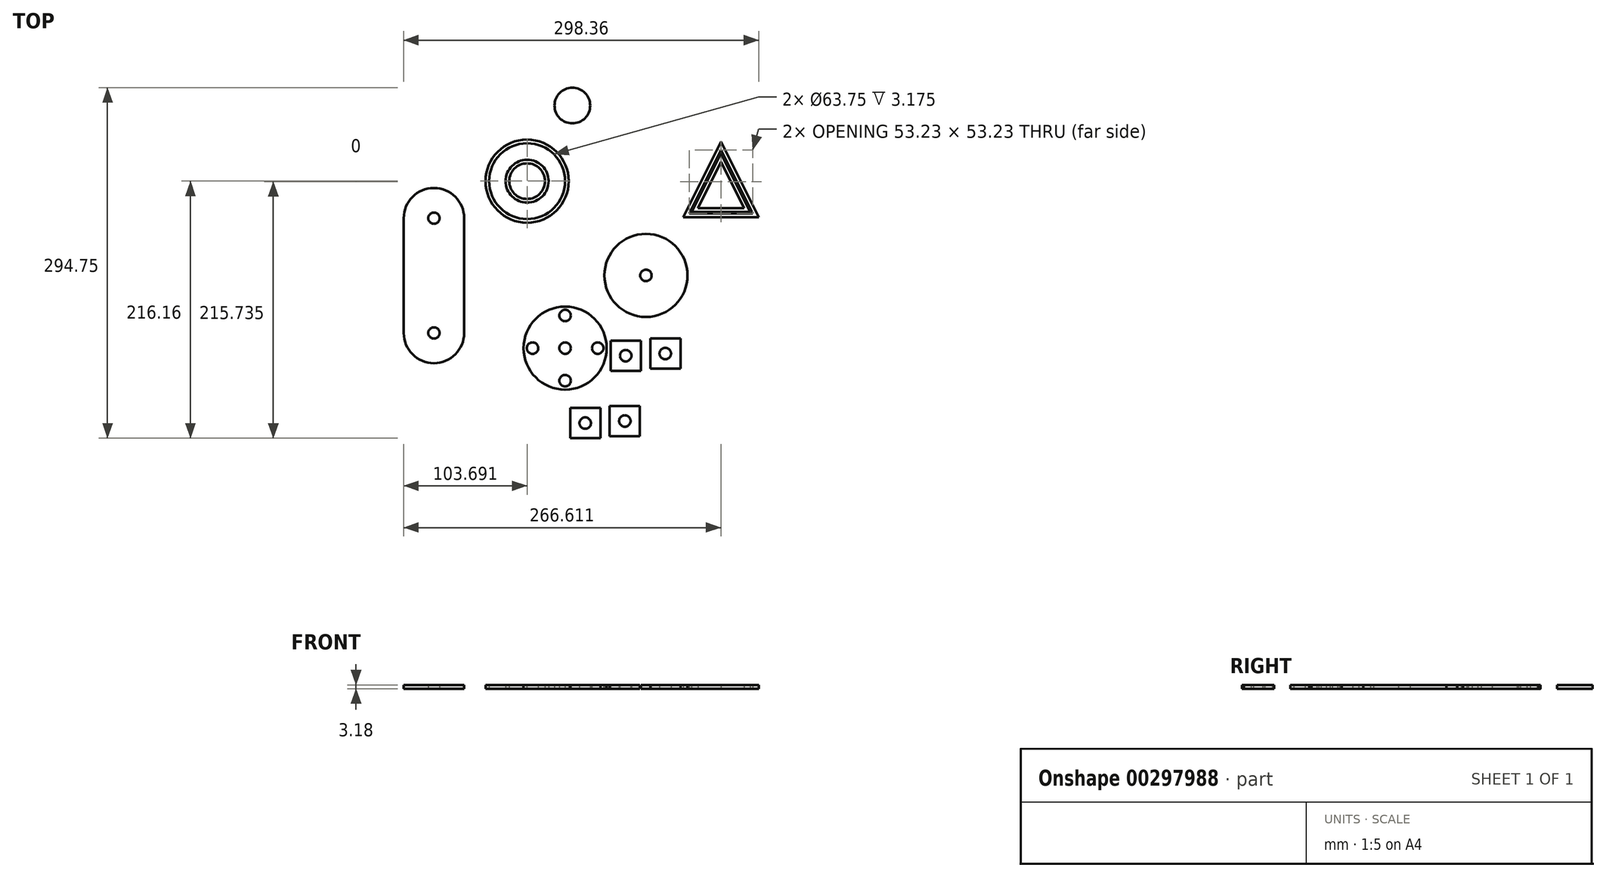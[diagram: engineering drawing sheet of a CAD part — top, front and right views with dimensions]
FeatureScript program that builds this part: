
annotation { "Feature Type Name" : "Feature", "Feature Type Description" : "" }
export const myFeature = defineFeature(function(context is Context, id is Id, definition is map)
    precondition{}
    {
        {
            var Q0;
            Q0=qCreatedBy(makeId("Top.planeOp"),FACE);
            var sketch = newSketch(context, id + "F0", { "sketchPlane" : qUnion([Q0])});
            skLineSegment(sketch, "E0", {"start": v(57.75, 2.39) * mm, "end": v(121.25, 2.39) * mm});
            skLineSegment(sketch, "E1", {"start": v(57.75, 2.39) * mm, "end": v(89.5, 65.89) * mm});
            skPoint(sketch, "E1.endSnap0", {"position": v(89.5, 2.39) * mm});
            skLineSegment(sketch, "E2", {"start": v(89.5, 65.89) * mm, "end": v(121.25, 2.39) * mm});
            skLineSegment(sketch, "E3", {"start": v(116.11, 5.56) * mm, "end": v(89.5, 58.79) * mm});
            skLineSegment(sketch, "E4", {"start": v(62.89, 5.56) * mm, "end": v(116.11, 5.56) * mm});
            skLineSegment(sketch, "E5", {"start": v(89.5, 58.79) * mm, "end": v(62.89, 5.56) * mm});
            skLineSegment(sketch, "E6", {"start": v(64.94, 6.83) * mm, "end": v(114.06, 6.83) * mm});
            skLineSegment(sketch, "E7", {"start": v(64.94, 6.83) * mm, "end": v(89.5, 55.95) * mm});
            skLineSegment(sketch, "E8", {"start": v(89.5, 55.95) * mm, "end": v(114.06, 6.83) * mm});
            skLineSegment(sketch, "E9", {"start": v(70.08, 10) * mm, "end": v(89.5, 48.85) * mm});
            skLineSegment(sketch, "E10", {"start": v(89.5, 48.85) * mm, "end": v(108.92, 10) * mm});
            skLineSegment(sketch, "E11", {"start": v(108.92, 10) * mm, "end": v(70.08, 10) * mm});
            skPoint(sketch, "E12.start.orphan", {"position": v(76.2, 32.18) * mm});
            skPoint(sketch, "E13.end.orphan", {"position": v(89.5, 5.56) * mm});
            skPoint(sketch, "E14.end.orphan", {"position": v(80.88, 6.83) * mm});
            skPoint(sketch, "E15.end.orphan", {"position": v(94.24, 10) * mm});
            skCircle(sketch, "E16", {"center": v(-73.42, 32.6) * mm, "radius": 34.95 * mm});
            skCircle(sketch, "E17", {"center": v(-73.42, 32.6) * mm, "radius": 31.88 * mm});
            skLineSegment(sketch, "E18", {"start": v(89.5, 48.85) * mm, "end": v(89.5, 10) * mm});
            skCircle(sketch, "E19", {"center": v(-73.42, 32.6) * mm, "radius": 18.03 * mm});
            skCircle(sketch, "E20", {"center": v(-73.42, 32.6) * mm, "radius": 14.99 * mm});
            skLineSegment(sketch, "E21", {"start": v(89.5, 2.39) * mm, "end": v(89.5, 5.56) * mm});
            skLineSegment(sketch, "E22", {"start": v(89.5, 6.83) * mm, "end": v(89.5, 48.85) * mm});
            skCircle(sketch, "E23", {"center": v(-35.38, 96.2) * mm, "radius": 14.99 * mm});
            skSolve(sketch);
        }
        {
            var Q0;
            Q0=qCreatedBy(makeId("Top.planeOp"),FACE);
            var sketch = newSketch(context, id + "F1", { "sketchPlane" : qUnion([Q0])});
            skCircle(sketch, "E24", {"center": v(-41.46, -107.8) * mm, "radius": 34.93 * mm});
            skCircle(sketch, "E25", {"center": v(-41.46, -107.8) * mm, "radius": 4.83 * mm});
            skPoint(sketch, "E26.orphan", {"position": v(-46.28, -107.8) * mm});
            skPoint(sketch, "E27.orphan", {"position": v(-36.63, -107.8) * mm});
            skPoint(sketch, "E28.orphan", {"position": v(-41.46, -112.63) * mm});
            skPoint(sketch, "E29.orphan", {"position": v(-41.46, -102.98) * mm});
            skPoint(sketch, "E30", {"position": v(-41.46, -135.2) * mm});
            skPoint(sketch, "E31", {"position": v(-14.06, -107.8) * mm});
            skPoint(sketch, "E32", {"position": v(-41.46, -80.4) * mm});
            skPoint(sketch, "E33", {"position": v(-68.86, -107.8) * mm});
            skPoint(sketch, "E34.trimOffspring.end.orphan", {"position": v(-76.38, -107.8) * mm});
            skPoint(sketch, "E35.end.orphan", {"position": v(-41.46, -72.88) * mm});
            skPoint(sketch, "E36.end.orphan", {"position": v(-6.53, -107.8) * mm});
            skPoint(sketch, "E37.trimOffspring.end.orphan", {"position": v(-41.46, -142.73) * mm});
            skCircle(sketch, "E38", {"center": v(-41.46, -135.2) * mm, "radius": 4.83 * mm});
            skCircle(sketch, "E39", {"center": v(-14.06, -107.8) * mm, "radius": 4.83 * mm});
            skCircle(sketch, "E40", {"center": v(-41.46, -80.4) * mm, "radius": 4.83 * mm});
            skCircle(sketch, "E41", {"center": v(-68.86, -107.8) * mm, "radius": 4.83 * mm});
            skLineSegment(sketch, "E42", {"start": v(-41.46, -112.63) * mm, "end": v(-41.46, -102.98) * mm});
            skSolve(sketch);
        }
        {
            var Q0;
            Q0=makeQuery(id+"F1.imprint","IMPRINT",FACE,{"disambiguationData":[TD([[makeQuery(id+"F1.imprint","IMPRINT",EDGE,{"derivedFrom":sQuery(id+"F1.wireOp",EDGE,"E24")}),1.0]])]});
            extrude(context, id + "F2", {"entities" : qUnion([Q0]), "depth" : 3.17 * mm});
        }
        {
            var Q0;
            Q0=qCreatedBy(makeId("Top.planeOp"),FACE);
            var sketch = newSketch(context, id + "F3", { "sketchPlane" : qUnion([Q0])});
            skCircle(sketch, "E43", {"center": v(26.47, -46.67) * mm, "radius": 34.93 * mm});
            skSolve(sketch);
        }
        {
            var Q0;
            Q0=makeQuery(id+"F3.imprint","IMPRINT",FACE,{"disambiguationData":[TD([[makeQuery(id+"F3.imprint","IMPRINT",EDGE,{"derivedFrom":sQuery(id+"F3.wireOp",EDGE,"E43")}),1.0]])]});
            extrude(context, id + "F4", {"entities" : qUnion([Q0]), "depth" : 3.17 * mm});
        }
        {
            var Q0;
            Q0=makeQuery(id+"F4.opExtrude","CAP_FACE",FACE,{"disambiguationData":[OSD([sQuery(id+"F3.wireOp",EDGE,"E43")])],"isStart":false});
            var sketch = newSketch(context, id + "F5", { "sketchPlane" : qUnion([Q0])});
            skPoint(sketch, "E44", {"position": v(26.47, -46.67) * mm});
            skCircle(sketch, "E45", {"center": v(26.47, -46.67) * mm, "radius": 4.83 * mm});
            skSolve(sketch);
        }
        {
            var Q0;
            Q0=makeQuery(id+"F5.imprint","IMPRINT",FACE,{"disambiguationData":[TD([[makeQuery(id+"F5.imprint","IMPRINT",EDGE,{"derivedFrom":sQuery(id+"F5.wireOp",EDGE,"E45")}),1.0]])]});
            extrude(context, id + "F6", {"entities" : qUnion([Q0]), "operationType" : NewBodyOperationType.REMOVE, "oppositeDirection" : true, "depth" : 25.4 * mm});
        }
        {
            var Q0;
            Q0=qCreatedBy(makeId("Top.planeOp"),FACE);
            var sketch = newSketch(context, id + "F7", { "sketchPlane" : qUnion([Q0])});
            skLineSegment(sketch, "E46.bottom", {"start": v(-3.27, -101.45) * mm, "end": v(22.13, -101.45) * mm});
            skLineSegment(sketch, "E46.top", {"start": v(-3.27, -126.85) * mm, "end": v(22.13, -126.85) * mm});
            skLineSegment(sketch, "E46.left", {"start": v(-3.27, -101.45) * mm, "end": v(-3.27, -126.85) * mm});
            skLineSegment(sketch, "E46.right", {"start": v(22.13, -101.45) * mm, "end": v(22.13, -126.85) * mm});
            skPoint(sketch, "E47", {"position": v(9.43, -114.15) * mm});
            skCircle(sketch, "E48", {"center": v(9.43, -114.15) * mm, "radius": 4.83 * mm});
            skLineSegment(sketch, "E49.MirrorCS", {"start": v(30.02, -99.66) * mm, "end": v(30.02, -125.06) * mm});
            skLineSegment(sketch, "E50.MirrorCS", {"start": v(55.42, -99.66) * mm, "end": v(30.02, -99.66) * mm});
            skLineSegment(sketch, "E51.MirrorCS", {"start": v(55.42, -125.06) * mm, "end": v(30.02, -125.06) * mm});
            skLineSegment(sketch, "E52.MirrorCS", {"start": v(55.42, -99.66) * mm, "end": v(55.42, -125.06) * mm});
            skPoint(sketch, "E53", {"position": v(42.72, -112.36) * mm});
            skCircle(sketch, "E54", {"center": v(42.72, -112.36) * mm, "radius": 4.83 * mm});
            skLineSegment(sketch, "E55.bottom", {"start": v(-37.27, -158.16) * mm, "end": v(-11.87, -158.16) * mm});
            skLineSegment(sketch, "E55.top", {"start": v(-37.27, -183.56) * mm, "end": v(-11.87, -183.56) * mm});
            skLineSegment(sketch, "E55.left", {"start": v(-37.27, -158.16) * mm, "end": v(-37.27, -183.56) * mm});
            skLineSegment(sketch, "E55.right", {"start": v(-11.87, -158.16) * mm, "end": v(-11.87, -183.56) * mm});
            skPoint(sketch, "E56", {"position": v(-24.57, -170.86) * mm});
            skCircle(sketch, "E57", {"center": v(-24.57, -170.86) * mm, "radius": 4.83 * mm});
            skLineSegment(sketch, "E58.MirrorCS", {"start": v(-3.97, -156.37) * mm, "end": v(-3.97, -181.77) * mm});
            skLineSegment(sketch, "E59.MirrorCS", {"start": v(21.43, -156.37) * mm, "end": v(-3.97, -156.37) * mm});
            skLineSegment(sketch, "E60.MirrorCS", {"start": v(21.43, -181.77) * mm, "end": v(-3.97, -181.77) * mm});
            skLineSegment(sketch, "E61.MirrorCS", {"start": v(21.43, -156.37) * mm, "end": v(21.43, -181.77) * mm});
            skPoint(sketch, "E62", {"position": v(8.73, -169.07) * mm});
            skCircle(sketch, "E63", {"center": v(8.73, -169.07) * mm, "radius": 4.83 * mm});
            skSolve(sketch);
        }
        {
            var Q0;
            Q0=makeQuery(id+"F7.imprint","IMPRINT",FACE,{"disambiguationData":[TD([[makeQuery(id+"F7.imprint","IMPRINT",EDGE,{"derivedFrom":sQuery(id+"F7.wireOp",EDGE,"E46.bottom")}),-1.0]])]});
            var Q1;
            Q1=makeQuery(id+"F7.imprint","IMPRINT",FACE,{"disambiguationData":[TD([[makeQuery(id+"F7.imprint","IMPRINT",EDGE,{"derivedFrom":sQuery(id+"F7.wireOp",EDGE,"xvH5cVz1-pj4Y-tES7-m2WN-IS9xY6hBvVlf.bottom")}),-1.0]])]});
            var Q2;
            Q2=makeQuery(id+"F7.imprint","IMPRINT",FACE,{"disambiguationData":[TD([[makeQuery(id+"F7.imprint","IMPRINT",EDGE,{"derivedFrom":sQuery(id+"F7.wireOp",EDGE,"6ae7865e-581d-49da-b914-e63cb27099890.MirrorC")}),1.0]])]});
            extrude(context, id + "F8", {"entities" : qUnion([Q0, Q1, Q2]), "depth" : 3.17 * mm});
        }
        {
            var Q0;
            Q0=makeQuery(id+"F0.imprint","IMPRINT",FACE,{"disambiguationData":[TD([[makeQuery(id+"F0.imprint","IMPRINT",EDGE,{"derivedFrom":sQuery(id+"F0.wireOp",EDGE,"E19")}),1.0]])]});
            var Q1;
            Q1=makeQuery(id+"F0.imprint","IMPRINT",FACE,{"disambiguationData":[TD([[makeQuery(id+"F0.imprint","IMPRINT",EDGE,{"derivedFrom":sQuery(id+"F0.wireOp",EDGE,"E16")}),1.0]])]});
            var Q2;
            Q2=makeQuery(id+"F0.imprint","IMPRINT",FACE,{"disambiguationData":[TD([[makeQuery(id+"F0.imprint","IMPRINT",EDGE,{"derivedFrom":sQuery(id+"F0.wireOp",EDGE,"E0")}),1.0]])]});
            var Q3;
            Q3=makeQuery(id+"F0.imprint","IMPRINT",FACE,{"disambiguationData":[TD([[makeQuery(id+"F0.imprint","IMPRINT",EDGE,{"derivedFrom":sQuery(id+"F0.wireOp",EDGE,"E6")}),1.0]])]});
            extrude(context, id + "F9", {"entities" : qUnion([Q0, Q1, Q2, Q3]), "depth" : 3.17 * mm});
        }
        {
            var Q0;
            Q0=qCreatedBy(makeId("Top.planeOp"),FACE);
            var sketch = newSketch(context, id + "F10", { "sketchPlane" : qUnion([Q0])});
            skArc(sketch, "E64", {"start": v(-126.31, 1.47) * mm, "mid": v(-151.71, 26.87) * mm, "end": v(-177.11, 1.47) * mm});
            skLineSegment(sketch, "E65", {"start": v(-177.11, 1.47) * mm, "end": v(-177.11, -95.05) * mm});
            skArc(sketch, "E66", {"start": v(-177.11, -95.05) * mm, "mid": v(-151.71, -120.45) * mm, "end": v(-126.31, -95.05) * mm});
            skLineSegment(sketch, "E67", {"start": v(-126.31, 1.47) * mm, "end": v(-126.31, -95.05) * mm});
            skCircle(sketch, "E68", {"center": v(-151.71, 1.47) * mm, "radius": 4.76 * mm});
            skCircle(sketch, "E69", {"center": v(-151.71, -95.05) * mm, "radius": 4.76 * mm});
            skSolve(sketch);
        }
        {
            var Q0;
            Q0=makeQuery(id+"F10.imprint","IMPRINT",FACE,{"disambiguationData":[TD([[makeQuery(id+"F10.imprint","IMPRINT",EDGE,{"derivedFrom":sQuery(id+"F10.wireOp",EDGE,"E64")}),1.0]])]});
            extrude(context, id + "F11", {"entities" : qUnion([Q0]), "depth" : 3.17 * mm});
        }
        {
            var Q0;
            Q0=qSketchRegion(id+"F7",true);
            extrude(context, id + "F12", {"entities" : qUnion([Q0]), "operationType" : NewBodyOperationType.ADD, "depth" : 3.17 * mm});
        }
        {
            var Q0;
            Q0=qSketchRegion(id+"F0",true);
            extrude(context, id + "F13", {"entities" : qUnion([Q0]), "depth" : 3.17 * mm});
        }
    });
